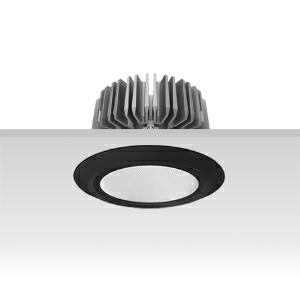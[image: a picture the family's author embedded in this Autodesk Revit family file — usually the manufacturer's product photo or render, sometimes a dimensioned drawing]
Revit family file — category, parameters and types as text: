
# Revit family: 3f_filippi_-_3f_reno_bianco_ampio_3f_filippi_-_30387_a01047_-_3f_reno_150_wh_3000-930_dali_wide___smp_bk_86ab
name_source: partatom
category: Lighting Fixtures
units: mm (PartAtom-declared; Revit-internal decimal feet)

## family parameters
Cut with Voids When Loaded = No
Host = Face
Light Source = No
Part Type = Normal
Room Calculation Point = No
Round Connector Dimension = Use Diameter
Shared = No

## types (1)
- 3F Filippi - 3F Reno Bianco Ampio (1 x LED, 2324 lm, 37 W, 3000 K)
    Apparent Load = 37 VA
    Approval mark = CE
    CIE Flux Codes = 73 92 98 100 100
    Color Rendering = 90
    Color Temperature = 3000 K
    Control Gear = Electronic transformer
    Default Elevation = 1800 mm
    Description = ILLUMINOTECHNICAL
Luminous efficiency 100% (DLOR 100%, ULOR 0%).
Initial luminous flux of the luminaire 2324 lm.
Direct symmetric wide distribution.
Installation Interdistance Transv.D = 1.01 x hu - Long.D = 1.00 x hu.
Tabular UGR (CIE 117 - 4H-8H; S=0.25H; 70/50/20): RUG 24.5 - 24.5.
Beam angle: 70° - 70°.
Luminous efficacy 63 lm/W.
Lifetime (L90/B10): 30000 h. (tq+25°C)
Lifetime (L85/B10): 50000 h. (tq+25°C)
Lifetime (L70/B10): 80000 h. (tq+25°C)
Sudden decreased luminous flux after 50000 hours: 0% (C0).
Photobiological safety in compliance with IEC/TR 62778: RG0 risk exempt, (IEC 62471).
In compliance with IEC/EN 62722-2-1 - IEC/EN 62717 standards.

SOURCE
Compact LED module 3000/930.
Energy efficiency class (UE 2019/2020 - UE 2019/2015): F.
CIE 13.3 Colour rendering index: CRI >90 (R9 >50%).
IES TM-30 Fidelity Index: Rf = 92 Rg = 101.
CCT nominal colour temperature 3000 K.
Colour initial tolerance (MacAdam): SDCM 3.
Zhaga Book 3 compliant.

MECHANICAL
Passive heat dissipator in die-casting aluminium, oversized, for optimum thermal management of the LED module.
Parabolic element with graduated/concentric rings in white polycarbonate.
Transparent external lens with glossy and satin differentiated surfaces, with a cooling and anti-insect system in methacrylate (PMMA).
Fastening spring clips in stainless steel.
Dimensions: diameter 176 mm, height 111 mm. Weight 1.45 kg.
IP44 protection degree for exposed part, IP20 for recessed part.
Mechanical strength to impacts IK05 (0.7 joule).
Glow-wire test resistance 650°C.

ELECTRICAL
Wiring on a separate unit.
Halogen Free DALI-2 DATI (Parts 251, 252, 253), PUSH-DIM, electronic wiring 230V-50/60Hz, power factor 0.97 at full load, THD <25%, constant output current, SELV, class II, 1 driver, 1 DALI addresse.
Power of the luminaire 37 W.
ENEC - CE.
SAFE FLICKER: PstLM=<1 and SVM=<0.4 (IEC TR 61547-1 and IEC TR 63158), to ensure a more comfortable and safe light.
Luminaire compliant with EN 60598-2-22 for power supply from a centralised emergency system CPSS (Central Power Supply System), not incorporated in the luminaire - high risk areas excluded. The default power and flux are 100% in AC and 100% in DC.
Ambient temperature from 0°C to +25°C.
Temperature class T6 max 85°C.
Relative humidity UR: <85%.

INSTALLATION
Pull-up recessed fitting.
False ceiling carving: 150 mm.
All accessories dedicated to this product are available on the Catalog and on our website www.3F-Filippi.com.

ACCESSORIES
A01047 - Anti-glare microprismatic SMP diffuser in methacrylate (PMMA), locked and in line with the trim, in black polycarbonate.

APPLICATIONS
Suitable product for food production plants (HACCP), IFS (Food Version 6), BRC (GSFS Food Version 7).
Environments: architectural, commercial, exhibition areas, transit areas, corridors, shops, display windows, service areas.
In false ceilings with narrow voids.

LIGHT MANAGEMENT
Recommended minimum setting: 10%.
The luminaire, equipped with (DALI-2 DATI) driver, can be controlled manually with 3F Easy Dim technology or automatically/manually with wired or wireless DALI/D2D control systems.
The D2D driver guarantees interoperability with other devices with the same certification by making the following information available:
Device Data (Part 251), Energy Report (Part 252), Diagnosis & Maintenance (Part 253).
In electrical systems without a regulation system (manual or automatic) and DALI bus, a suitable jumper must be made on the DA-DA terminals of the appliance.

WARNING
Luminaire designed for disposal/recycling at end-of-life.
Replaceable (LED only) light source by a professional. Replaceable control gear by a professional.
    Height = 0 mm  [stored 0 ft]
    Lamp = 1 x LED
    Lamp Light Flux = 2324 lm
    Lamp Power = 37 W
    Lamp count = 1
    Length = 176 mm
    Lifetime = 50000 h
    Luminous efficacy = 63 lm/W
    Manufacturer = 3F Filippi
    ModVariant = No
    Model = 3F Filippi - 30387+A01047 - 3F Reno 150 WH 3000-930 DALI WIDE + SMP BK
    Mounting Place = Ceiling
    Mounting Type = Recessed
    Number of Poles = 1
    OnlyDefault = Yes
    Power Factor = 1
    Product Name = 3F Filippi - 3F Reno Bianco Ampio
    Product group = recessed luminaire
    ProductGroupID = 4
    Protection Class = Protection class II
    Protection Degree = IP 20
    RLX_Detail_Level = 1
    RLX_Emergency_Light_Flux = 0 lm
    RLX_Emergency_Type = 0
    RLX_Emergency_Type_DB = No
    RlxData = <blob elided: 88265 chars, md5=597628b0>
    Socket = socket
    Standby Power = 0 W
    System Light Flux = 2324 lm
    System Power = 37 W
    Type Comments = Product without accessories
    Type Image = 3ffilippi_3f_reno_150_bk_vs_smp.jpg
    URL = http://relux.com
    VarID = ---
    Voltage = 0 V
    Weight = 0.00 kg
    Width = 0 mm  [stored 0 ft]

note: [stored X ft] marks values corroborated as IEEE doubles in the binary element streams (Revit-internal decimal feet)

## geometry (parser evidence)
native form markers: Blend x4, Sweep x11
no freeform markers — native parametric forms only
